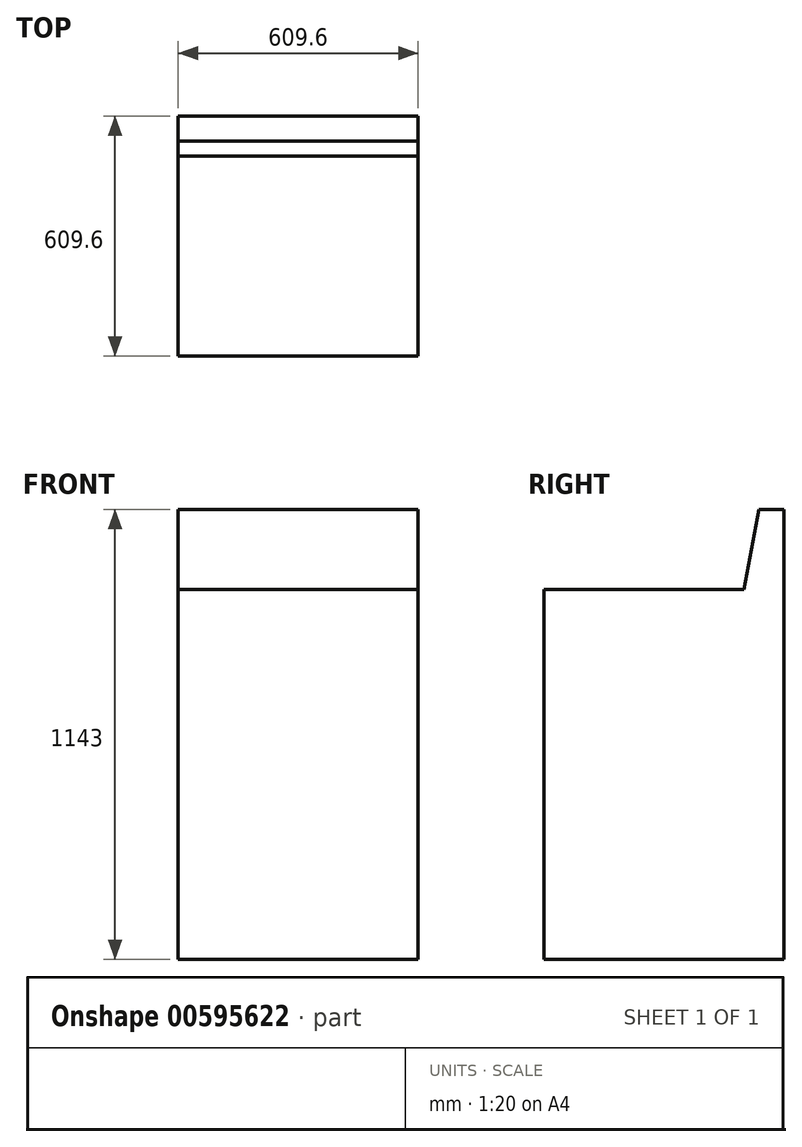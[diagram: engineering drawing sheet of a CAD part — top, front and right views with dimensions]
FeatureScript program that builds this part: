
annotation { "Feature Type Name" : "Feature", "Feature Type Description" : "" }
export const myFeature = defineFeature(function(context is Context, id is Id, definition is map)
    precondition{}
    {
        {
            var Q0;
            Q0=qCreatedBy(makeId("Right.planeOp"),FACE);
            var sketch = newSketch(context, id + "F0", { "sketchPlane" : qUnion([Q0])});
            skLineSegment(sketch, "E0.bottom", {"start": v(0, 0) * mm, "end": v(609.6, 0) * mm});
            skLineSegment(sketch, "E0.top", {"start": v(0, 939.8) * mm, "end": v(609.6, 939.8) * mm});
            skLineSegment(sketch, "E0.left", {"start": v(0, 0) * mm, "end": v(0, 939.8) * mm});
            skLineSegment(sketch, "E0.right", {"start": v(609.6, 0) * mm, "end": v(609.6, 939.8) * mm});
            skLineSegment(sketch, "E1.bottom", {"start": v(609.6, 939.8) * mm, "end": v(508, 939.8) * mm});
            skLineSegment(sketch, "E1.top", {"start": v(609.6, 1143) * mm, "end": v(546.1, 1143) * mm});
            skLineSegment(sketch, "E1.left", {"start": v(609.6, 939.8) * mm, "end": v(609.6, 1143) * mm});
            skLineSegment(sketch, "E2", {"start": v(508, 939.8) * mm, "end": v(546.1, 1143) * mm});
            skSolve(sketch);
        }
        {
            var Q0;
            Q0=qSketchRegion(id+"F0",true);
            extrude(context, id + "F1", {"entities" : qUnion([Q0]), "depth" : 609.6 * mm, "offsetDistance" : 25.4 * mm});
        }
    });
